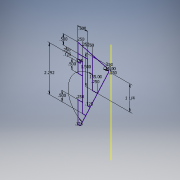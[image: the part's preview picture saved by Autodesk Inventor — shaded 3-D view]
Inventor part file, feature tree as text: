
AUTODESK INVENTOR PART (.ipt)
format: ipt  version: 2017 (Build 210142000, 142)  size: 113,152 bytes
history: native  units: in
note: dims shown in document units (in); Inventor stores cm internally (conversion verified against a paired STEP export)
features: sketch x1
ambient origin geometry x8: Origin, YZ Plane, XZ Plane, XY Plane, X Axis, Y Axis, Z Axis, Center Point
feature tree (1):
  sketch  "Sketch1"  dims[d0=0.25in d1=0.1718in d2=15.0deg d4=0.25in d5=1.5in d6=1.25in d7=0.25in d11=0.25in d13=0.5in d15=0.25in d16=0.25in d18=0.125in d19=0.5in d20=0.125in d21=0.25in d22=0.125in d23=0.125in d24=0.25in d25=0.5in d26=2.292in d27=0.5in]
